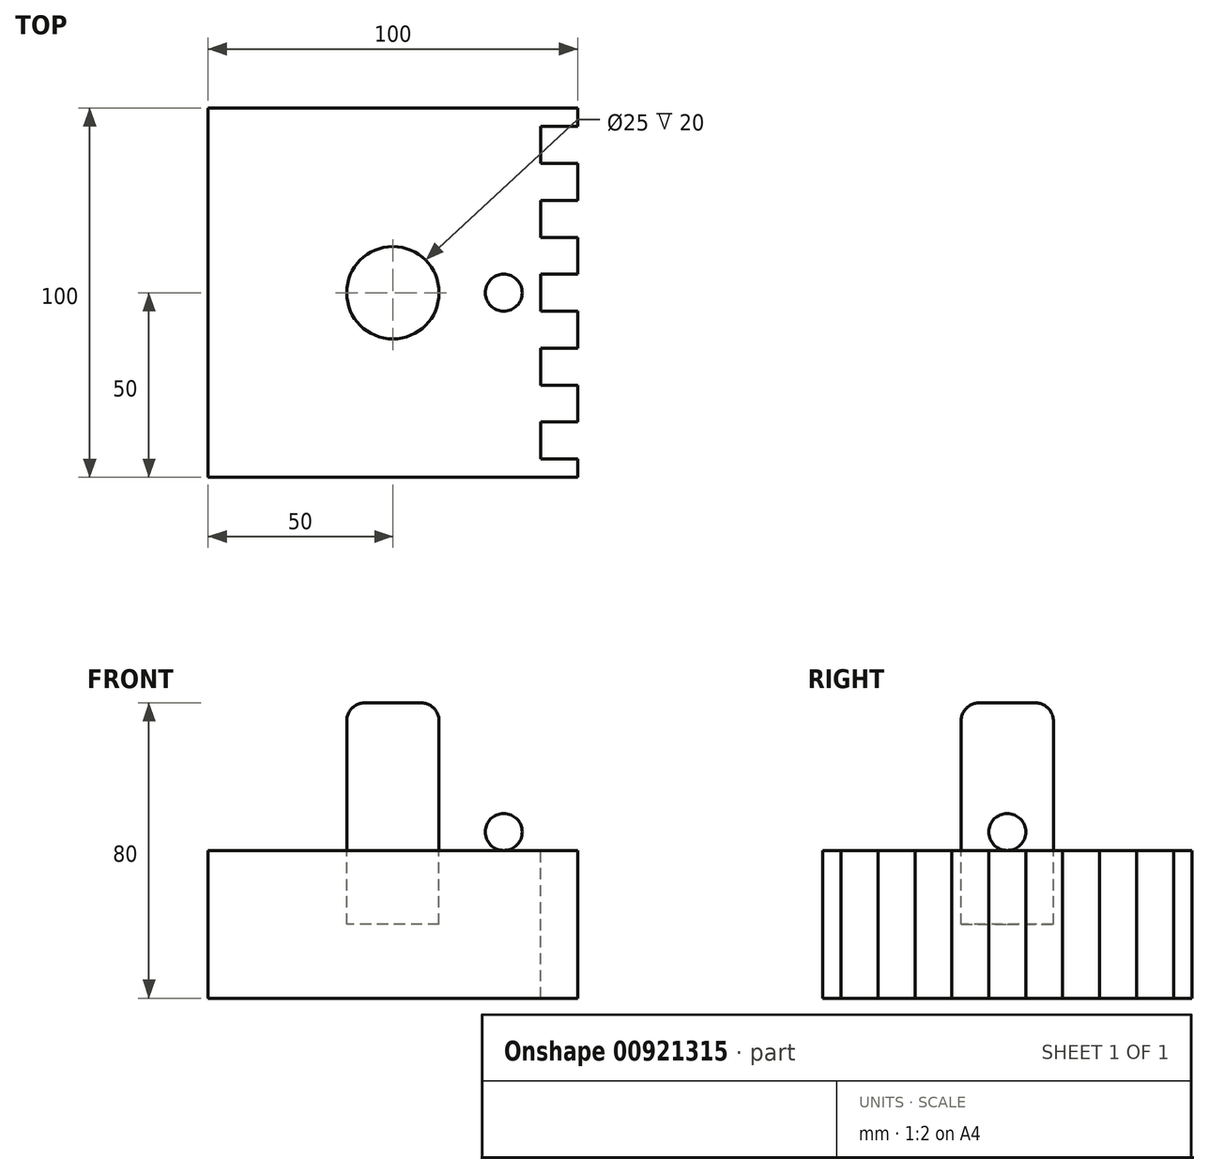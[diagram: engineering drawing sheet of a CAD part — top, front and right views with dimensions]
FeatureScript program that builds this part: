
annotation { "Feature Type Name" : "Feature", "Feature Type Description" : "" }
export const myFeature = defineFeature(function(context is Context, id is Id, definition is map)
    precondition{}
    {
        {
            var Q0;
            Q0=qCreatedBy(makeId("Top.planeOp"),FACE);
            var sketch = newSketch(context, id + "F0", { "sketchPlane" : qUnion([Q0])});
            skLineSegment(sketch, "E0.bottom", {"start": v(50, -50) * mm, "end": v(-50, -50) * mm});
            skLineSegment(sketch, "E0.top", {"start": v(50, 50) * mm, "end": v(-50, 50) * mm});
            skLineSegment(sketch, "E0.left", {"start": v(50, -50) * mm, "end": v(50, 50) * mm});
            skLineSegment(sketch, "E0.right", {"start": v(-50, -50) * mm, "end": v(-50, 50) * mm});
            skPoint(sketch, "E0.middle", {"position": v(0, 0) * mm});
            skSolve(sketch);
        }
        {
            var Q0;
            Q0=makeQuery(id+"F0.imprint","IMPRINT",FACE,{"disambiguationData":[TD([[makeQuery(id+"F0.imprint","IMPRINT",EDGE,{"derivedFrom":sQuery(id+"F0.wireOp",EDGE,"E0.bottom")}),-1.0]])]});
            extrude(context, id + "F1", {"entities" : qUnion([Q0]), "depth" : 40 * mm, "offsetDistance" : 25 * mm});
        }
        {
            var Q0;
            Q0=qCreatedBy(makeId("Top.planeOp"),FACE);
            cPlane(context, id + "F2", {"entities" : qUnion([Q0]), "cplaneType" : CPlaneType.OFFSET, "offset" : 40 * mm, "width" : 150 * mm, "height" : 150 * mm});
        }
        {
            var Q0;
            Q0=qCreatedBy(id+"F2.planeOp",FACE);
            var sketch = newSketch(context, id + "F3", { "sketchPlane" : qUnion([Q0])});
            skCircle(sketch, "E1", {"center": v(0, 0) * mm, "radius": 12.5 * mm});
            skSolve(sketch);
        }
        {
            var Q0;
            Q0 = qSketchRegion(id + "F3", true);
            extrude(context, id + "F4", {"entities" : qUnion([Q0]), "operationType" : NewBodyOperationType.REMOVE, "oppositeDirection" : true, "depth" : 20 * mm, "offsetDistance" : 25 * mm});
        }
        {
            var Q0;
            Q0 = qSketchRegion(id + "F3", true);
            extrude(context, id + "F5", {"entities" : qUnion([Q0]), "depth" : 40 * mm, "offsetDistance" : 25 * mm});
        }
        {
            var Q0;
            Q0=makeQuery(id+"F5.opExtrude","CAP_FACE",FACE,{"disambiguationData":[OSD([sQuery(id+"F3.wireOp",EDGE,"E1")])],"isStart":false});
            fillet(context, id + "F6", {"entities" : qUnion([Q0]), "radius" : 5 * mm, "tangentPropagation" : true, "allowEdgeOverflow" : false});
        }
        {
            var Q0;
            Q0=makeQuery(id+"F1.opExtrude","CAP_FACE",FACE,{"disambiguationData":[OSD([sQuery(id+"F0.wireOp",EDGE,"E0.bottom"),sQuery(id+"F0.wireOp",EDGE,"E0.top"),sQuery(id+"F0.wireOp",EDGE,"E0.left"),sQuery(id+"F0.wireOp",EDGE,"E0.right")])],"isStart":false});
            var sketch = newSketch(context, id + "F7", { "sketchPlane" : qUnion([Q0])});
            skLineSegment(sketch, "E2", {"start": v(50, 45) * mm, "end": v(40, 45) * mm});
            skLineSegment(sketch, "E3", {"start": v(40, 45) * mm, "end": v(40, 35) * mm});
            skLineSegment(sketch, "E4", {"start": v(40, 35) * mm, "end": v(50, 35) * mm});
            skLineSegment(sketch, "E5.1.0.0", {"start": v(50, 25) * mm, "end": v(40, 25) * mm});
            skLineSegment(sketch, "E5.1.0.1", {"start": v(40, 25) * mm, "end": v(40, 15) * mm});
            skLineSegment(sketch, "E5.1.0.2", {"start": v(40, 15) * mm, "end": v(50, 15) * mm});
            skLineSegment(sketch, "E5.2.0.0", {"start": v(50, 5) * mm, "end": v(40, 5) * mm});
            skLineSegment(sketch, "E5.2.0.1", {"start": v(40, 5) * mm, "end": v(40, -5) * mm});
            skLineSegment(sketch, "E5.2.0.2", {"start": v(40, -5) * mm, "end": v(50, -5) * mm});
            skLineSegment(sketch, "E5.direction1", {"start": v(40, 45) * mm, "end": v(40, 25) * mm, "construction": true});
            skLineSegment(sketch, "E6.0.3.0", {"start": v(50, -15) * mm, "end": v(40, -15) * mm});
            skLineSegment(sketch, "E6.3.3.0", {"start": v(40, -15) * mm, "end": v(40, -25) * mm});
            skLineSegment(sketch, "E6.6.3.0", {"start": v(40, -25) * mm, "end": v(50, -25) * mm});
            skLineSegment(sketch, "E6.0.4.0", {"start": v(50, -35) * mm, "end": v(40, -35) * mm});
            skLineSegment(sketch, "E6.3.4.0", {"start": v(40, -35) * mm, "end": v(40, -45) * mm});
            skLineSegment(sketch, "E6.6.4.0", {"start": v(40, -45) * mm, "end": v(50, -45) * mm});
            skSolve(sketch);
        }
        {
            var Q0;
            {var subQ0=sQuery(id+"F7.wireOp",EDGE,"E2");Q0=makeQuery(id+"F7.imprint","IMPRINT",FACE,{"disambiguationData":[TD([[makeQuery(id+"F7.imprint","IMPRINT",EDGE,{"derivedFrom":subQ0}),1.0]])]});}
            var Q1;
            {var subQ0=sQuery(id+"F7.wireOp",EDGE,"E5.1.0.0");Q1=makeQuery(id+"F7.imprint","IMPRINT",FACE,{"disambiguationData":[TD([[makeQuery(id+"F7.imprint","IMPRINT",EDGE,{"derivedFrom":subQ0}),1.0]])]});}
            var Q2;
            {var subQ0=sQuery(id+"F7.wireOp",EDGE,"E5.2.0.0");Q2=makeQuery(id+"F7.imprint","IMPRINT",FACE,{"disambiguationData":[TD([[makeQuery(id+"F7.imprint","IMPRINT",EDGE,{"derivedFrom":subQ0}),1.0]])]});}
            var Q3;
            {var subQ0=sQuery(id+"F7.wireOp",EDGE,"E6.0.3.0");Q3=makeQuery(id+"F7.imprint","IMPRINT",FACE,{"disambiguationData":[TD([[makeQuery(id+"F7.imprint","IMPRINT",EDGE,{"derivedFrom":subQ0}),1.0]])]});}
            var Q4;
            {var subQ0=sQuery(id+"F7.wireOp",EDGE,"E6.0.4.0");Q4=makeQuery(id+"F7.imprint","IMPRINT",FACE,{"disambiguationData":[TD([[makeQuery(id+"F7.imprint","IMPRINT",EDGE,{"derivedFrom":subQ0}),1.0]])]});}
            var Q5;
            {var subQ0=sQuery(id+"F7.wireOp",EDGE,"E6.0.5.0");Q5=makeQuery(id+"F7.imprint","IMPRINT",FACE,{"disambiguationData":[TD([[makeQuery(id+"F7.imprint","IMPRINT",EDGE,{"derivedFrom":subQ0}),1.0]])]});}
            var Q6;
            {var subQ0=sQuery(id+"F7.wireOp",EDGE,"E6.0.6.0");Q6=makeQuery(id+"F7.imprint","IMPRINT",FACE,{"disambiguationData":[TD([[makeQuery(id+"F7.imprint","IMPRINT",EDGE,{"derivedFrom":subQ0}),1.0]])]});}
            var Q7;
            {var subQ0=sQuery(id+"F7.wireOp",EDGE,"E6.0.7.0");Q7=makeQuery(id+"F7.imprint","IMPRINT",FACE,{"disambiguationData":[TD([[makeQuery(id+"F7.imprint","IMPRINT",EDGE,{"derivedFrom":subQ0}),1.0]])]});}
            var Q8;
            {var subQ0=sQuery(id+"F7.wireOp",EDGE,"E6.0.8.0");Q8=makeQuery(id+"F7.imprint","IMPRINT",FACE,{"disambiguationData":[TD([[makeQuery(id+"F7.imprint","IMPRINT",EDGE,{"derivedFrom":subQ0}),1.0]])]});}
            var Q9;
            {var subQ0=sQuery(id+"F7.wireOp",EDGE,"E6.0.9.0");Q9=makeQuery(id+"F7.imprint","IMPRINT",FACE,{"disambiguationData":[TD([[makeQuery(id+"F7.imprint","IMPRINT",EDGE,{"derivedFrom":subQ0}),1.0]])]});}
            extrude(context, id + "F8", {"entities" : qUnion([Q0, Q1, Q2, Q3, Q4, Q5, Q6, Q7, Q8, Q9]), "operationType" : NewBodyOperationType.REMOVE, "oppositeDirection" : true, "depth" : 40 * mm, "offsetDistance" : 25 * mm});
        }
        {
            var Q0;
            Q0=qCreatedBy(id+"F2.planeOp",FACE);
            var sketch = newSketch(context, id + "F9", { "sketchPlane" : qUnion([Q0])});
            skCircle(sketch, "E7", {"center": v(30, 0) * mm, "radius": 5 * mm});
            skSolve(sketch);
        }
        {
            var Q0;
            Q0 = qSketchRegion(id + "F9", true);
            extrude(context, id + "F10", {"entities" : qUnion([Q0]), "depth" : 10 * mm, "offsetDistance" : 25 * mm});
        }
        {
            var Q0;
            Q0=makeQuery(id+"F10.opExtrude","CAP_EDGE",EDGE,{"disambiguationData":[OSD([sQuery(id+"F9.wireOp",EDGE,"E7")])],"isStart":false});
            var Q1;
            Q1=makeQuery(id+"F10.opExtrude","SWEPT_FACE",FACE,{"disambiguationData":[OSD([sQuery(id+"F9.wireOp",EDGE,"E7")])]});
            fillet(context, id + "F11", {"entities" : qUnion([Q0, Q1]), "radius" : 5 * mm, "tangentPropagation" : true, "allowEdgeOverflow" : false});
        }
    });
